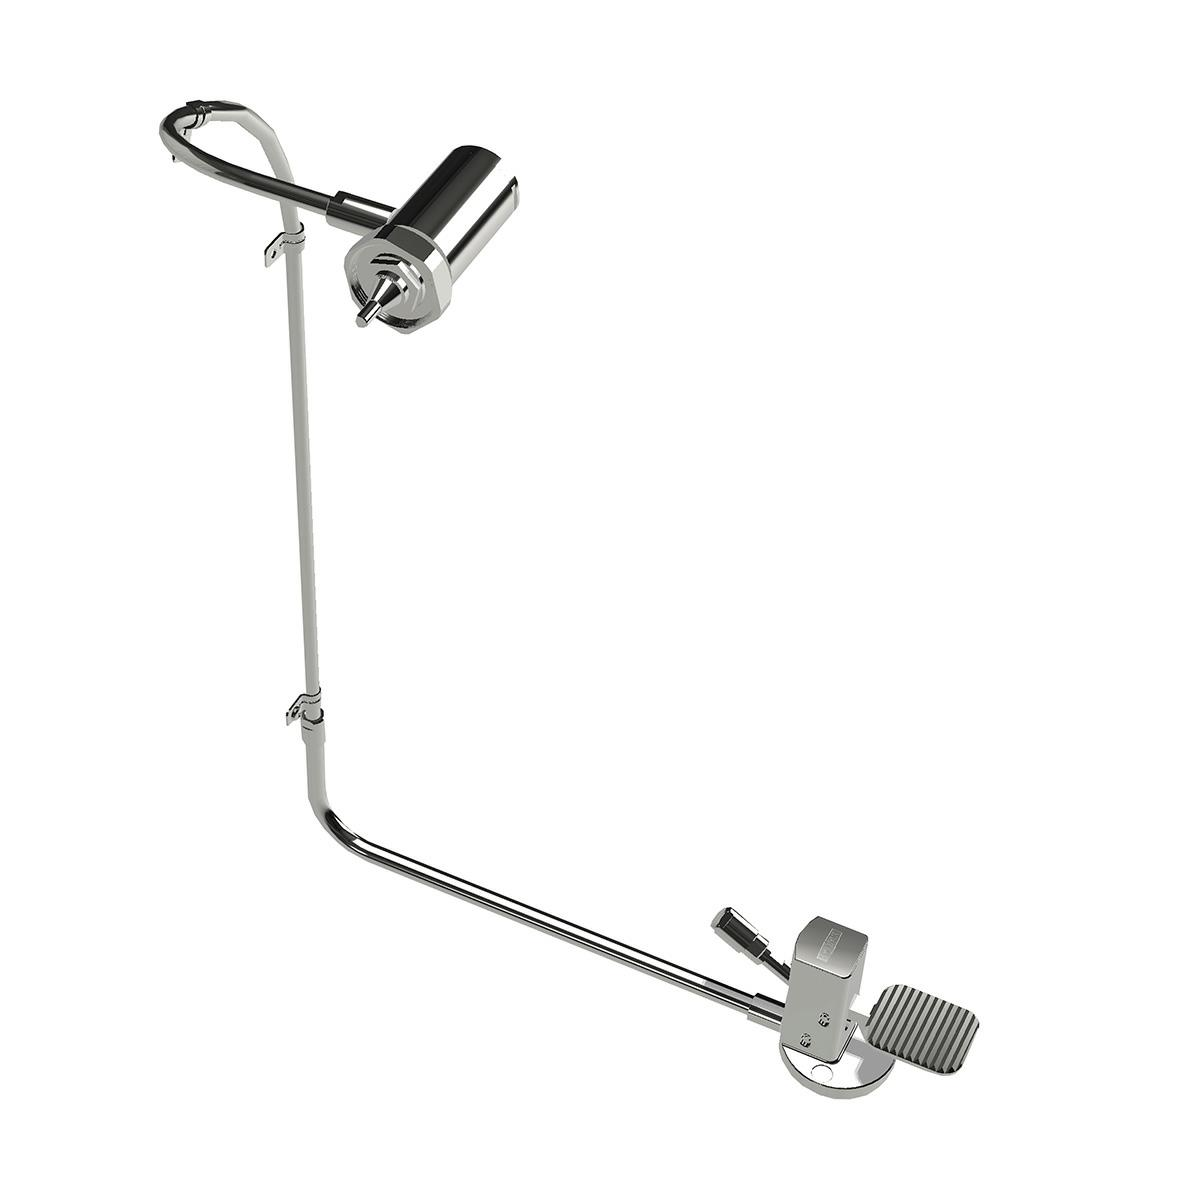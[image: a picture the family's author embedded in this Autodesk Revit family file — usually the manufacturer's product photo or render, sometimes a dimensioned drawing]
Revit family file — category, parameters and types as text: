
# Revit family: KFP-1
name_source: partatom
category: Aparatos sanitarios
units: mm (PartAtom-declared; Revit-internal decimal feet)

## family parameters
Compartido = Sí
Corte con vacíos al cargar = No
Cota de conector redondo = Diámetro de uso
Número OmniClass = 23.45.00.00
Punto de cálculo de habitación = No
Se basa en plano de trabajo = No
Siempre vertical = Sí
Tipo de pieza = Normal
Título OmniClass = Sanitary, Laundry, and Cleaning Equipment

## types (1)
- KFP-1
    Chrome = Brass Chromed
    Comentarios de tipo = Kit fluxómetro de manija a pedal expuesto
    Conexión AF = Sí
    Descripción = Kit fluxómetro de manija a pedal expuesto
    Documentation = https://www.helvex.com.mx
    Elevación por defecto = 0"
    Fabricante = HELVEX
    Imagen de tipo = KFP-1.jpg
    Instructive = https://www.helvex.com.mx
    Modelo = KFP-1
    Note = Doblar tubo flexible con radio mínimo a 10 cm.
Máximo 3 dobleces.
    URL = https://www.helvex.com.mx

## geometry (parser evidence)
native form markers: Sweep x3
no freeform markers — native parametric forms only
